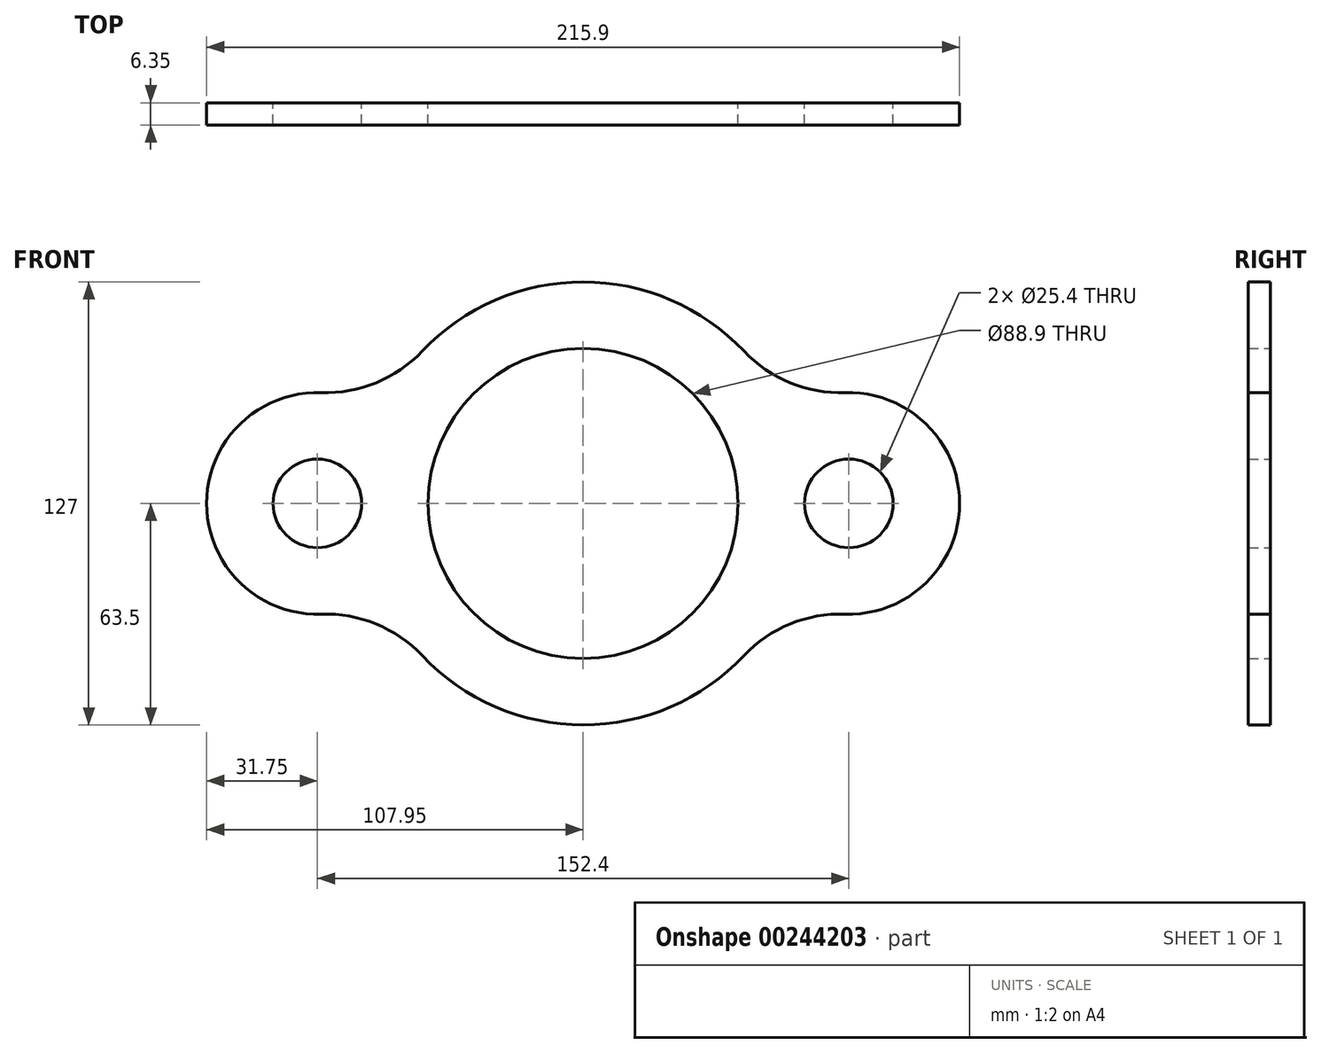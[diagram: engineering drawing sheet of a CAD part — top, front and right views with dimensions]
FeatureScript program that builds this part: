
annotation { "Feature Type Name" : "Feature", "Feature Type Description" : "" }
export const myFeature = defineFeature(function(context is Context, id is Id, definition is map)
    precondition{}
    {
        {
            var Q0;
            Q0=qCreatedBy(makeId("Front.planeOp"),FACE);
            var sketch = newSketch(context, id + "F0", { "sketchPlane" : qUnion([Q0])});
            skArc(sketch, "E0", {"start": v(-46.14, -43.63) * mm, "mid": v(0, -63.5) * mm, "end": v(46.14, -43.63) * mm});
            skCircle(sketch, "E1", {"center": v(0, 0) * mm, "radius": 44.45 * mm});
            skArc(sketch, "E2", {"start": v(75.12, -31.73) * mm, "mid": v(107.95, 0) * mm, "end": v(75.12, 31.73) * mm});
            skCircle(sketch, "E3", {"center": v(76.2, 0) * mm, "radius": 12.7 * mm});
            skArc(sketch, "E4", {"start": v(-75.12, 31.73) * mm, "mid": v(-107.95, 0) * mm, "end": v(-75.12, -31.73) * mm});
            skCircle(sketch, "E5", {"center": v(-76.2, 0) * mm, "radius": 12.7 * mm});
            skArc(sketch, "E6.trimOffspring", {"start": v(46.14, 43.63) * mm, "mid": v(0, 63.5) * mm, "end": v(-46.14, 43.63) * mm});
            skPoint(sketch, "E7.visualSharp", {"position": v(-57.94, 25.98) * mm});
            skArc(sketch, "E7.filletArc", {"start": v(-75.12, 31.73) * mm, "mid": v(-59.35, 34.56) * mm, "end": v(-46.14, 43.63) * mm});
            skPoint(sketch, "E8.visualSharp", {"position": v(-57.94, -25.98) * mm});
            skArc(sketch, "E8.filletArc", {"start": v(-46.14, -43.63) * mm, "mid": v(-59.35, -34.56) * mm, "end": v(-75.12, -31.73) * mm});
            skPoint(sketch, "E9.visualSharp", {"position": v(57.94, -25.98) * mm});
            skArc(sketch, "E9.filletArc", {"start": v(75.12, -31.73) * mm, "mid": v(59.35, -34.56) * mm, "end": v(46.14, -43.63) * mm});
            skPoint(sketch, "E10.visualSharp", {"position": v(57.94, 25.98) * mm});
            skArc(sketch, "E10.filletArc", {"start": v(46.14, 43.63) * mm, "mid": v(59.35, 34.56) * mm, "end": v(75.12, 31.73) * mm});
            skSolve(sketch);
        }
        {
            var Q0;
            Q0=makeQuery(id+"F0.imprint","IMPRINT",FACE,{"disambiguationData":[TD([[makeQuery(id+"F0.imprint","IMPRINT",EDGE,{"derivedFrom":sQuery(id+"F0.wireOp",EDGE,"E0")}),1.0]])]});
            extrude(context, id + "F1", {"entities" : qUnion([Q0]), "depth" : 6.35 * mm});
        }
    });
